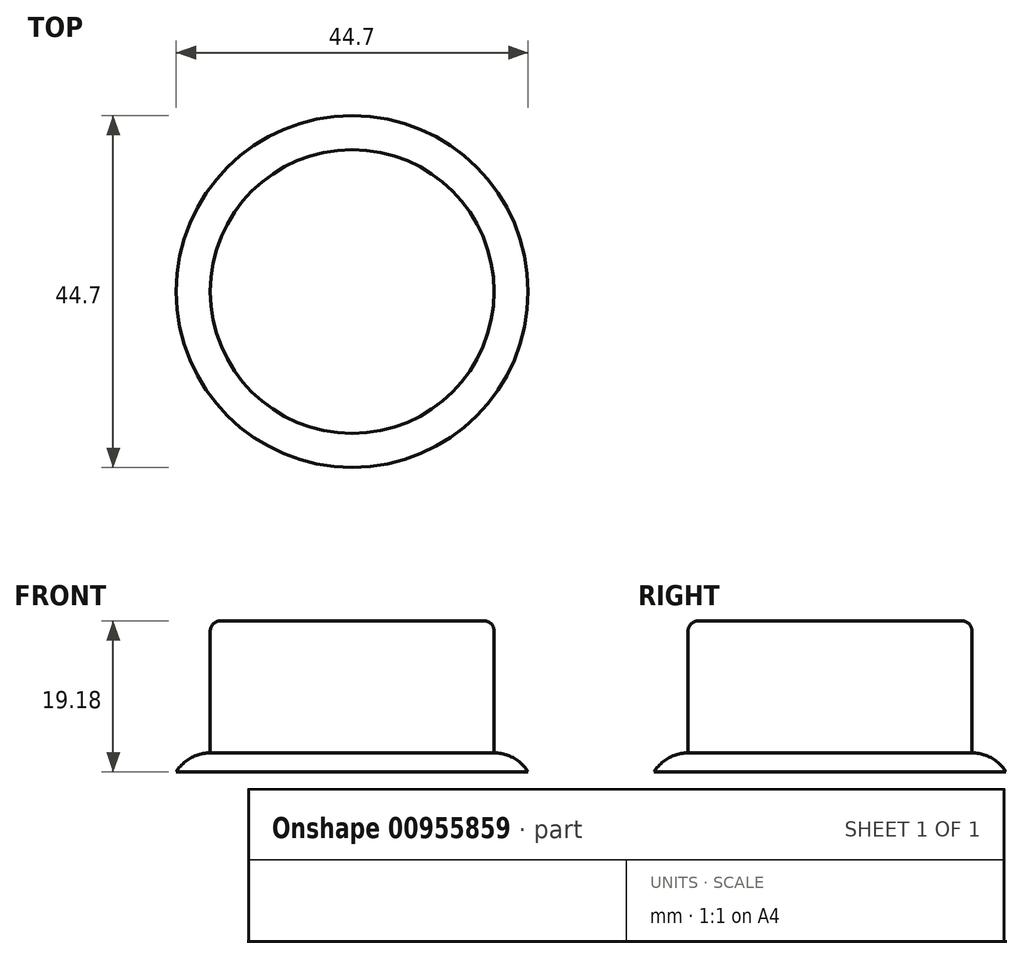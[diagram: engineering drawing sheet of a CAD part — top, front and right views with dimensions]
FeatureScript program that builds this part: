
annotation { "Feature Type Name" : "Feature", "Feature Type Description" : "" }
export const myFeature = defineFeature(function(context is Context, id is Id, definition is map)
    precondition{}
    {
        {
            var Q0;
            Q0=qCreatedBy(makeId("Top.planeOp"),FACE);
            var sketch = newSketch(context, id + "F0", { "sketchPlane" : qUnion([Q0])});
            skCircle(sketch, "E0", {"center": v(0, 0) * mm, "radius": 22.35 * mm});
            skSolve(sketch);
        }
        {
            var Q0;
            Q0=makeQuery(id+"F0.imprint","IMPRINT",FACE,{"disambiguationData":[TD([[makeQuery(id+"F0.imprint","IMPRINT",EDGE,{"derivedFrom":sQuery(id+"F0.wireOp",EDGE,"E0")}),1.0]])]});
            extrude(context, id + "F1", {"entities" : qUnion([Q0]), "depth" : 2.41 * mm, "offsetDistance" : 25.4 * mm});
        }
        {
            var Q0;
            Q0=makeQuery(id+"F1.opExtrude","CAP_EDGE",EDGE,{"disambiguationData":[OSD([sQuery(id+"F0.wireOp",EDGE,"E0")])],"isStart":false});
            fillet(context, id + "F2", {"entities" : qUnion([Q0]), "tangentPropagation" : true, "radius" : 5.08 * mm, "defaultsChanged" : false, "vertexSettings" : [], "allowEdgeOverflow" : false});
        }
        {
            var Q0;
            Q0=makeQuery(id+"F1.opExtrude","CAP_FACE",FACE,{"disambiguationData":[OSD([sQuery(id+"F0.wireOp",EDGE,"E0")])],"isStart":false});
            var sketch = newSketch(context, id + "F3", { "sketchPlane" : qUnion([Q0])});
            skCircle(sketch, "E1", {"center": v(0, 0) * mm, "radius": 18.29 * mm});
            skSolve(sketch);
        }
        {
            var Q0;
            {var subQ0=sQuery(id+"F0.wireOp",EDGE,"E0");Q0=makeQuery(id+"F3.imprint","IMPRINT",FACE,{"disambiguationData":[TD([[makeQuery(id+"F3.imprint","IMPRINT",EDGE,{"derivedFrom":makeQuery(id+"F2.opFillet","BLEND_EDGE",EDGE,{"blendedFrom":[makeQuery(id+"F1.opExtrude","CAP_EDGE",EDGE,{"disambiguationData":[OSD([subQ0])],"isStart":false}),makeQuery(id+"F1.opExtrude","CAP_FACE",FACE,{"disambiguationData":[OSD([subQ0])],"isStart":false})],"blendedInto":[makeQuery(id+"F1.opExtrude","CAP_FACE",FACE,{"disambiguationData":[OSD([subQ0])],"isStart":false})]})}),1.0]])]});}
            extrude(context, id + "F4", {"entities" : qUnion([Q0]), "operationType" : NewBodyOperationType.ADD, "depth" : 16.76 * mm, "offsetDistance" : 25.4 * mm});
        }
        {
            var Q0;
            Q0=makeQuery(id+"F4.opExtrude","CAP_EDGE",EDGE,{"disambiguationData":[OSD([sQuery(id+"F0.wireOp",EDGE,"E0")])],"isStart":false});
            fillet(context, id + "F5", {"entities" : qUnion([Q0]), "tangentPropagation" : true, "radius" : 1.27 * mm, "defaultsChanged" : true, "vertexSettings" : [], "allowEdgeOverflow" : false});
        }
    });
